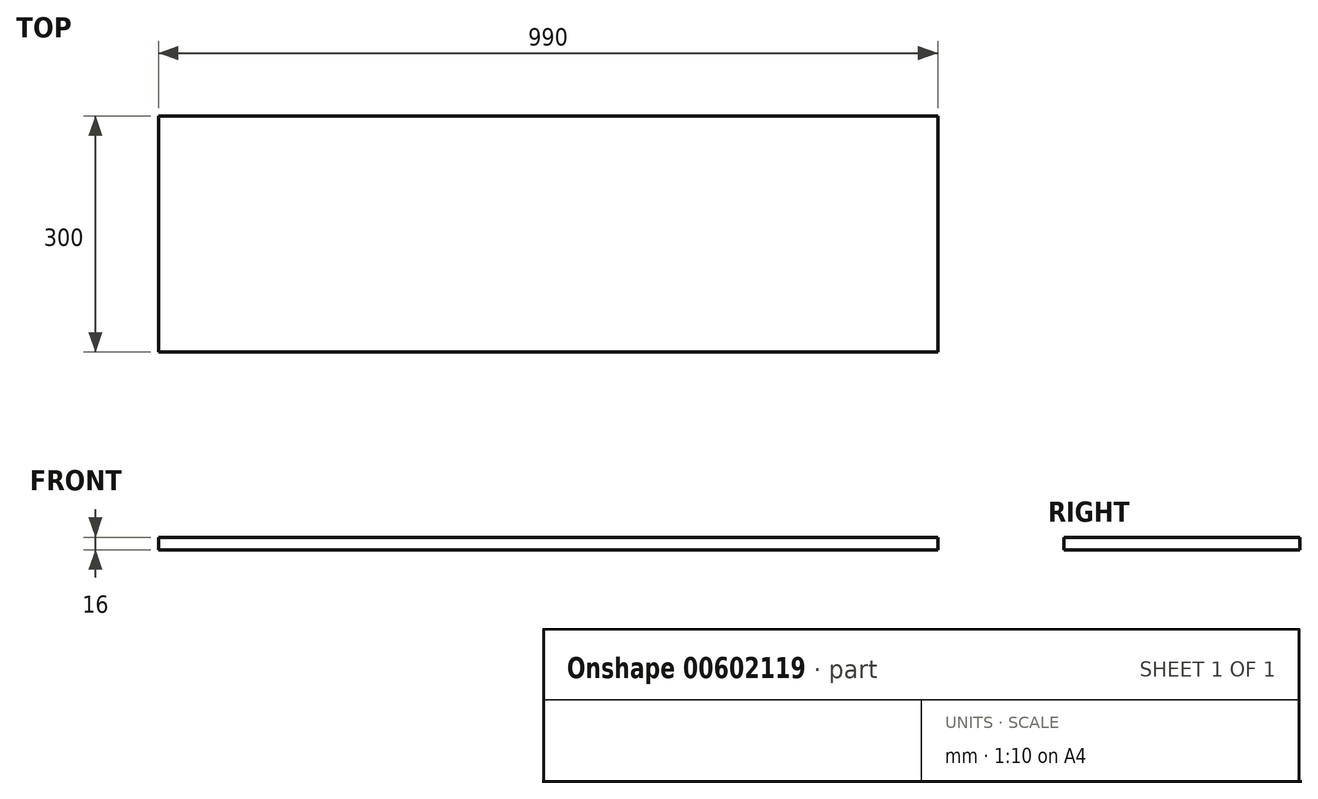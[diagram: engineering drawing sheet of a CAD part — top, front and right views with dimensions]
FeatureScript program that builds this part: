
annotation { "Feature Type Name" : "Feature", "Feature Type Description" : "" }
export const myFeature = defineFeature(function(context is Context, id is Id, definition is map)
    precondition{}
    {
        {
            var Q0;
            Q0=qCreatedBy(makeId("Top.planeOp"),FACE);
            var sketch = newSketch(context, id + "F0", { "sketchPlane" : qUnion([Q0])});
            skLineSegment(sketch, "E0.bottom", {"start": v(-990, -300) * mm, "end": v(0, -300) * mm});
            skLineSegment(sketch, "E0.top", {"start": v(-990, 0) * mm, "end": v(0, 0) * mm});
            skLineSegment(sketch, "E0.left", {"start": v(-990, -300) * mm, "end": v(-990, 0) * mm});
            skLineSegment(sketch, "E0.right", {"start": v(0, -300) * mm, "end": v(0, 0) * mm});
            skSolve(sketch);
        }
        {
            var Q0;
            Q0 = qSketchRegion(id + "F0", true);
            extrude(context, id + "F1", {"entities" : qUnion([Q0]), "depth" : 16 * mm, "offsetDistance" : 25 * mm});
        }
    });
